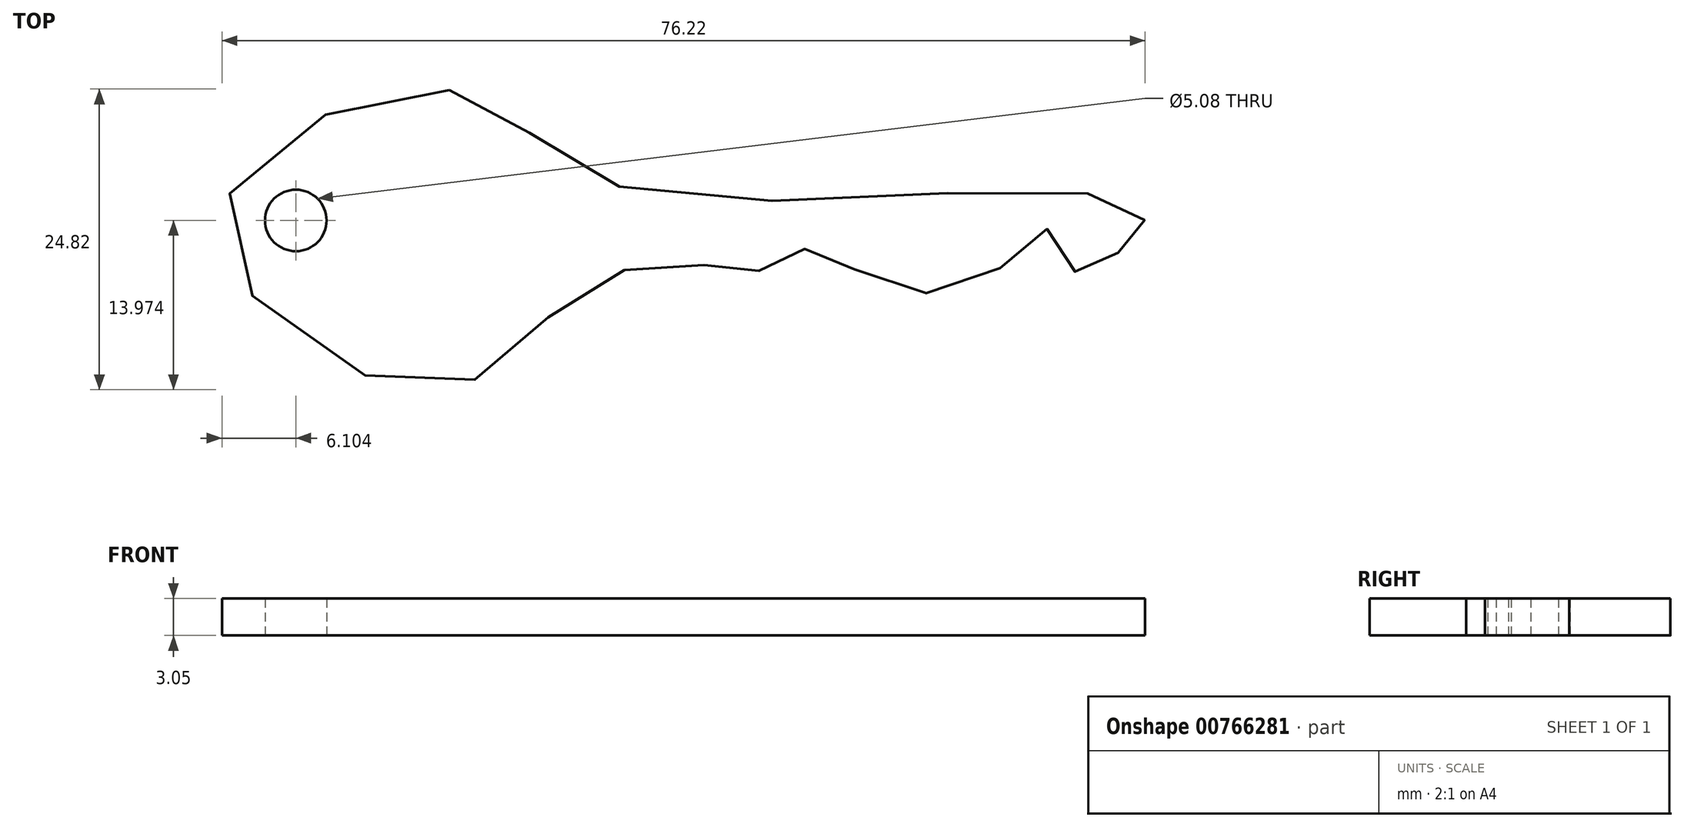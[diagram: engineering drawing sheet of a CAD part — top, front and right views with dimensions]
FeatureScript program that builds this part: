
annotation { "Feature Type Name" : "Feature", "Feature Type Description" : "" }
export const myFeature = defineFeature(function(context is Context, id is Id, definition is map)
    precondition{}
    {
        {
            var Q0;
            Q0=qCreatedBy(makeId("Top.planeOp"),FACE);
            var sketch = newSketch(context, id + "F0", { "sketchPlane" : qUnion([Q0])});
            skFitSpline(sketch, "E0", {"points": [v(-18.57, 22.85) * mm, v(-37.34, 12.05) * mm, v(-19.7, -1.88) * mm, v(-7.77, 6.36) * mm, v(2.72, 8.36) * mm, v(7.42, 8.02) * mm, v(11.17, 9.8) * mm, v(16.25, 7.27) * mm, v(25.64, 7.2) * mm, v(30.86, 11.36) * mm, v(33.18, 7.78) * mm, v(36.57, 9.37) * mm, v(38.86, 11.76) * mm, v(33.87, 14.34) * mm, v(-5.5, 15.18) * mm, v(-18.57, 22.85) * mm]});
            skCircle(sketch, "E1", {"center": v(-31.25, 12.08) * mm, "radius": 2.54 * mm});
            skSolve(sketch);
        }
        {
            var Q0;
            Q0=makeQuery(id+"F0.imprint","IMPRINT",FACE,{"disambiguationData":[TD([[makeQuery(id+"F0.imprint","IMPRINT",EDGE,{"derivedFrom":sQuery(id+"F0.wireOp",EDGE,"E0")}),1.0]])]});
            extrude(context, id + "F1", {"entities" : qUnion([Q0]), "depth" : 3.05 * mm, "offsetDistance" : 25.4 * mm});
        }
    });
